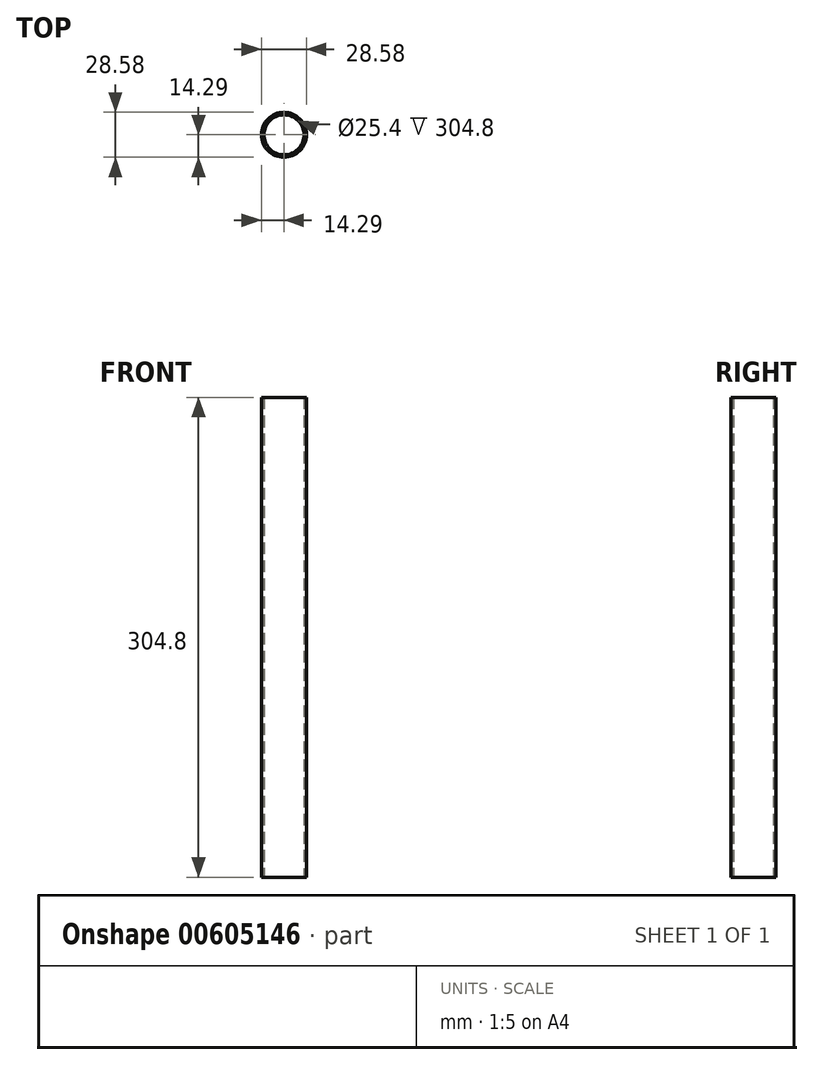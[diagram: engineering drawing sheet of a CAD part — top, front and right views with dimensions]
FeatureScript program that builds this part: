
annotation { "Feature Type Name" : "Feature", "Feature Type Description" : "" }
export const myFeature = defineFeature(function(context is Context, id is Id, definition is map)
    precondition{}
    {
        {
            var Q0;
            Q0=qCreatedBy(makeId("Top.planeOp"),FACE);
            var sketch = newSketch(context, id + "F0", { "sketchPlane" : qUnion([Q0])});
            skLineSegment(sketch, "E0", {"start": v(0, 0) * mm, "end": v(12.7, 0) * mm});
            skCircle(sketch, "E1", {"center": v(0, 0) * mm, "radius": 12.7 * mm});
            skCircle(sketch, "E2.0", {"center": v(0, 0) * mm, "radius": 14.29 * mm});
            skSolve(sketch);
        }
        {
            var Q0;
            Q0=qCreatedBy(makeId("Top.planeOp"),FACE);
            var sketch = newSketch(context, id + "F1", { "sketchPlane" : qUnion([Q0])});
            skSolve(sketch);
        }
        {
            var Q0;
            Q0=qSketchRegion(id+"F1",true);
            var Q1;
            Q1=makeQuery(id+"F0.imprint","IMPRINT",FACE,{"disambiguationData":[TD([[makeQuery(id+"F0.imprint","IMPRINT",EDGE,{"derivedFrom":sQuery(id+"F0.wireOp",EDGE,"E1")}),-1.0]])]});
            extrude(context, id + "F2", {"entities" : qUnion([Q0, Q1]), "depth" : 304.8 * mm, "offsetDistance" : 25.4 * mm});
        }
    });
